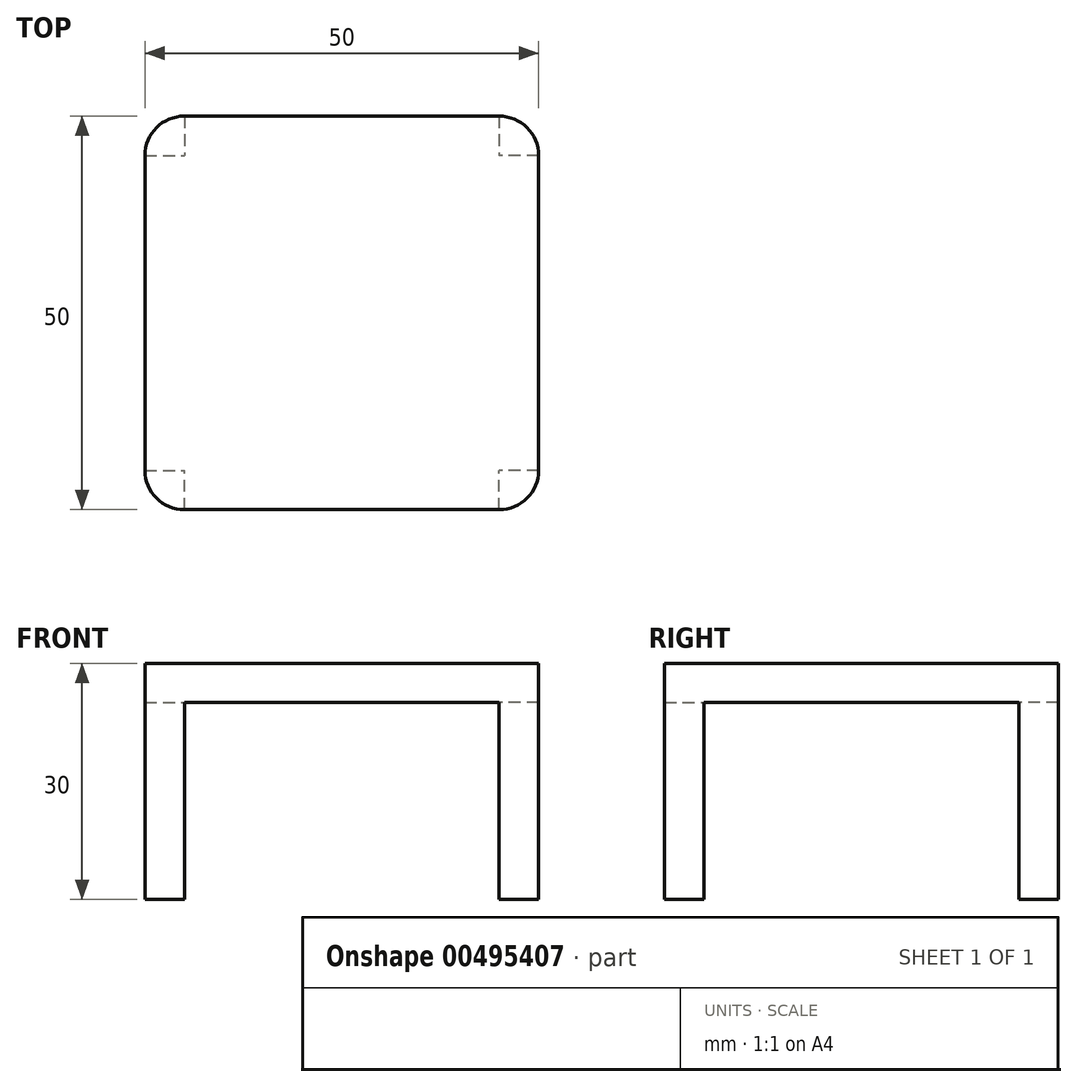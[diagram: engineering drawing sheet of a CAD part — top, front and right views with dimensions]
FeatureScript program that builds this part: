
annotation { "Feature Type Name" : "Feature", "Feature Type Description" : "" }
export const myFeature = defineFeature(function(context is Context, id is Id, definition is map)
    precondition{}
    {
        {
            var Q0;
            Q0=qCreatedBy(makeId("Front.planeOp"),FACE);
            var sketch = newSketch(context, id + "F0", { "sketchPlane" : qUnion([Q0])});
            skLineSegment(sketch, "E0.bottom", {"start": v(-25, 2.5) * mm, "end": v(25, 2.5) * mm});
            skLineSegment(sketch, "E0.top", {"start": v(-25, -2.5) * mm, "end": v(25, -2.5) * mm});
            skLineSegment(sketch, "E0.left", {"start": v(-25, 2.5) * mm, "end": v(-25, -2.5) * mm});
            skLineSegment(sketch, "E0.right", {"start": v(25, 2.5) * mm, "end": v(25, -2.5) * mm});
            skPoint(sketch, "E0.middle", {"position": v(0, 0) * mm});
            skSolve(sketch);
        }
        {
            var Q0;
            Q0=makeQuery(id+"F0.imprint","IMPRINT",FACE,{"disambiguationData":[TD([[makeQuery(id+"F0.imprint","IMPRINT",EDGE,{"derivedFrom":sQuery(id+"F0.wireOp",EDGE,"E0.bottom")}),-1.0]])]});
            extrude(context, id + "F1", {"entities" : qUnion([Q0]), "depth" : 50 * mm});
        }
        {
            var Q0;
            Q0=makeQuery(id+"F1.opExtrude","SWEPT_FACE",FACE,{"disambiguationData":[OSD([sQuery(id+"F0.wireOp",EDGE,"E0.top")])]});
            var sketch = newSketch(context, id + "F2", { "sketchPlane" : qUnion([Q0])});
            skLineSegment(sketch, "E1.bottom", {"start": v(-25, 50) * mm, "end": v(-20, 50) * mm});
            skLineSegment(sketch, "E1.top", {"start": v(-25, 45) * mm, "end": v(-20, 45) * mm});
            skLineSegment(sketch, "E1.left", {"start": v(-25, 50) * mm, "end": v(-25, 45) * mm});
            skLineSegment(sketch, "E1.right", {"start": v(-20, 50) * mm, "end": v(-20, 45) * mm});
            skLineSegment(sketch, "E2", {"start": v(0, -3.81) * mm, "end": v(0, 53.43) * mm, "construction": true});
            skPoint(sketch, "E2.endSnap0", {"position": v(0, 50) * mm});
            skLineSegment(sketch, "E3.bottom", {"start": v(-25, 0) * mm, "end": v(-20, 0) * mm});
            skLineSegment(sketch, "E3.top", {"start": v(-25, 5) * mm, "end": v(-20, 5) * mm});
            skLineSegment(sketch, "E3.left", {"start": v(-25, 0) * mm, "end": v(-25, 5) * mm});
            skLineSegment(sketch, "E3.right", {"start": v(-20, 0) * mm, "end": v(-20, 5) * mm});
            skLineSegment(sketch, "E4.MirrorCS", {"start": v(25, 45) * mm, "end": v(20, 45) * mm});
            skLineSegment(sketch, "E5.MirrorCS", {"start": v(20, 50) * mm, "end": v(20, 45) * mm});
            skLineSegment(sketch, "E6.MirrorCS", {"start": v(25, 50) * mm, "end": v(25, 45) * mm});
            skLineSegment(sketch, "E7.MirrorCS", {"start": v(25, 5) * mm, "end": v(20, 5) * mm});
            skLineSegment(sketch, "E8.MirrorCS", {"start": v(20, 0) * mm, "end": v(20, 5) * mm});
            skLineSegment(sketch, "E9.MirrorCS", {"start": v(25, 0) * mm, "end": v(25, 5) * mm});
            skLineSegment(sketch, "E10.MirrorCS", {"start": v(25, 0) * mm, "end": v(20, 0) * mm});
            skLineSegment(sketch, "E11.MirrorCS", {"start": v(25, 50) * mm, "end": v(20, 50) * mm});
            skSolve(sketch);
        }
        {
            var Q0;
            Q0=makeQuery(id+"F2.imprint","IMPRINT",FACE,{"disambiguationData":[TD([[makeQuery(id+"F2.imprint","IMPRINT",EDGE,{"derivedFrom":sQuery(id+"F2.wireOp",EDGE,"E1.bottom")}),-1.0]])]});
            var Q1;
            Q1=makeQuery(id+"F2.imprint","IMPRINT",FACE,{"disambiguationData":[TD([[makeQuery(id+"F2.imprint","IMPRINT",EDGE,{"derivedFrom":sQuery(id+"F2.wireOp",EDGE,"E4.MirrorCS")}),-1.0]])]});
            var Q2;
            Q2=makeQuery(id+"F2.imprint","IMPRINT",FACE,{"disambiguationData":[TD([[makeQuery(id+"F2.imprint","IMPRINT",EDGE,{"derivedFrom":sQuery(id+"F2.wireOp",EDGE,"E7.MirrorCS")}),1.0]])]});
            var Q3;
            Q3=makeQuery(id+"F2.imprint","IMPRINT",FACE,{"disambiguationData":[TD([[makeQuery(id+"F2.imprint","IMPRINT",EDGE,{"derivedFrom":sQuery(id+"F2.wireOp",EDGE,"E3.bottom")}),1.0]])]});
            extrude(context, id + "F3", {"entities" : qUnion([Q0, Q1, Q2, Q3]), "operationType" : NewBodyOperationType.ADD, "depth" : 25 * mm});
        }
        {
            var Q0;
            Q0=makeQuery(id+"F3.boolean.opBoolean","MERGE",EDGE,{"derivedFrom":[makeQuery(id+"F1.opExtrude","CAP_EDGE",EDGE,{"disambiguationData":[OSD([sQuery(id+"F0.wireOp",EDGE,"E0.left")])],"isStart":false}),makeQuery(id+"F3.opExtrude","SWEPT_EDGE",EDGE,{"disambiguationData":[OSD([sQuery(id+"F2.wireOp",EDGE,"E1.bottom"),sQuery(id+"F2.wireOp",EDGE,"E1.left")])]})]});
            var Q1;
            Q1=makeQuery(id+"F3.boolean.opBoolean","MERGE",EDGE,{"derivedFrom":[makeQuery(id+"F1.opExtrude","CAP_EDGE",EDGE,{"disambiguationData":[OSD([sQuery(id+"F0.wireOp",EDGE,"E0.right")])],"isStart":false}),makeQuery(id+"F3.opExtrude","SWEPT_EDGE",EDGE,{"disambiguationData":[OSD([sQuery(id+"F2.wireOp",EDGE,"E6.MirrorCS"),sQuery(id+"F2.wireOp",EDGE,"E11.MirrorCS")])]})]});
            var Q2;
            Q2=makeQuery(id+"F3.boolean.opBoolean","MERGE",EDGE,{"derivedFrom":[makeQuery(id+"F1.opExtrude","CAP_EDGE",EDGE,{"disambiguationData":[OSD([sQuery(id+"F0.wireOp",EDGE,"E0.right")])],"isStart":true}),makeQuery(id+"F3.opExtrude","SWEPT_EDGE",EDGE,{"disambiguationData":[OSD([sQuery(id+"F2.wireOp",EDGE,"E9.MirrorCS"),sQuery(id+"F2.wireOp",EDGE,"E10.MirrorCS")])]})]});
            var Q3;
            Q3=makeQuery(id+"F3.boolean.opBoolean","MERGE",EDGE,{"derivedFrom":[makeQuery(id+"F1.opExtrude","CAP_EDGE",EDGE,{"disambiguationData":[OSD([sQuery(id+"F0.wireOp",EDGE,"E0.left")])],"isStart":true}),makeQuery(id+"F3.opExtrude","SWEPT_EDGE",EDGE,{"disambiguationData":[OSD([sQuery(id+"F2.wireOp",EDGE,"E3.bottom"),sQuery(id+"F2.wireOp",EDGE,"E3.left")])]})]});
            fillet(context, id + "F4", {"entities" : qUnion([Q0, Q1, Q2, Q3]), "radius" : 5 * mm, "tangentPropagation" : true, "allowEdgeOverflow" : false});
        }
    });
